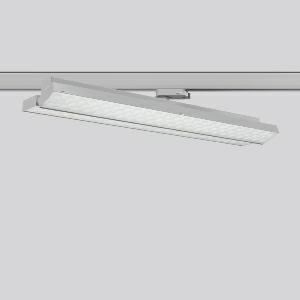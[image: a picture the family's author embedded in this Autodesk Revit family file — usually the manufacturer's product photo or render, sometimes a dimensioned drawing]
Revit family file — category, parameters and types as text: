
# Revit family: tx-move_742163_004_3_76_10b3
name_source: partatom
category: Lighting Fixtures
units: mm (PartAtom-declared; Revit-internal decimal feet)

## family parameters
Cut with Voids When Loaded = No
Host = Face
Light Source = No
Part Type = Normal
Room Calculation Point = No
Round Connector Dimension = Use Diameter
Shared = No

## types (1)
- MultiLumen 1 (1 x LED Modul 835, 2875 lm, 3500)
    Apparent Load = 41 VA
    CIE Flux Codes = 65 90 98 100 100
    Color Rendering = 80
    Color Temperature = 3500
    Default Elevation = 1800 mm
    Description = Series: TX-MOVE
Multifunctional surface-mounted spotlight for area lighting. Very flat design. Housing: sheet steel, powder-coated. Rotation range: 356°. Swivel range: 90°. Consistent alignment possible with visible tilt scale. High-efficiency LED units with optimum light control thanks to clear plastic (PC) lens optics. Spezielle Mikrostrukturen reduzieren Gelbsaum. Asymmetrical light distribution. With adapter for RZB 3-circuit DALI tracks. Suitable for Track on ceiling. MultiLumen: Luminous flux adjustable in 3 steps. Factory setting is the highest luminous flux. Environmentally friendly and resource-saving due to replaceable and recyclable components. 
Colour: silver, matt (approx. RAL 9006)
Length: 570 mm
Width: 119 mm
Height: 88 mm
Lamp: LED
Socket: without socket
Colour temperature: 3500K
Colour rendering index (CRI): 80
System power: 41 W
Rated luminous flux: 5750 lm
Luminous efficiency: 140 lm/W
System power 2: 57 W
Rated luminous flux 2: 7750 lm
Luminous efficiency 2: 136 lm/W
System power 3: 73 W
Rated luminous flux 3: 9450 lm
Luminous efficiency 3: 129 lm/W
Control gear: Dimmable EVG, DALI
Protection class: I
Type of protection: IP 20
    Height = 75 mm
    Lamp = 1 x LED Modul 835
    Lamp Light Flux = 2875 lm
    Lamp count = 1
    Length = 569 mm
    Lifetime = 50000 h
    Luminous efficacy = 140 lm/W
    Manufacturer = RZB
    ModVariant = No
    Model = 742163.004.3.76
    Mounting Place = Ceiling
    Mounting Type = Rail mounted
    Number of Poles = 1
    OnlyDefault = Yes
    Power Factor = 1
    Product Name = TX-MOVE
    Product group = Track mounted projectors
    ProductGroupID = 301
    Protection Class = Protection class I
    Protection Degree = IP 20
    RLX_Detail_Level = 1
    RLX_Emergency_Light_Flux = 0 lm
    RLX_Emergency_Type = 0
    RLX_Emergency_Type_DB = No
    RlxData = <blob elided: 53917 chars, md5=17406a5d>
    Socket = socket
    Standby Power = 0 W
    System Light Flux = 5750 lm
    System Power = 41 W
    Type Comments = MultiLumen 1
    Type Image = 742162.004.jpg
    URL = http://relux.com
    VarID = multilumen_1
    Voltage = 230 V
    Voltage Range = 220-240 V
    Weight = 0.00 kg
    Width = 119 mm

## geometry (parser evidence)
native form markers: Blend x4, Sweep x18
no freeform markers — native parametric forms only
